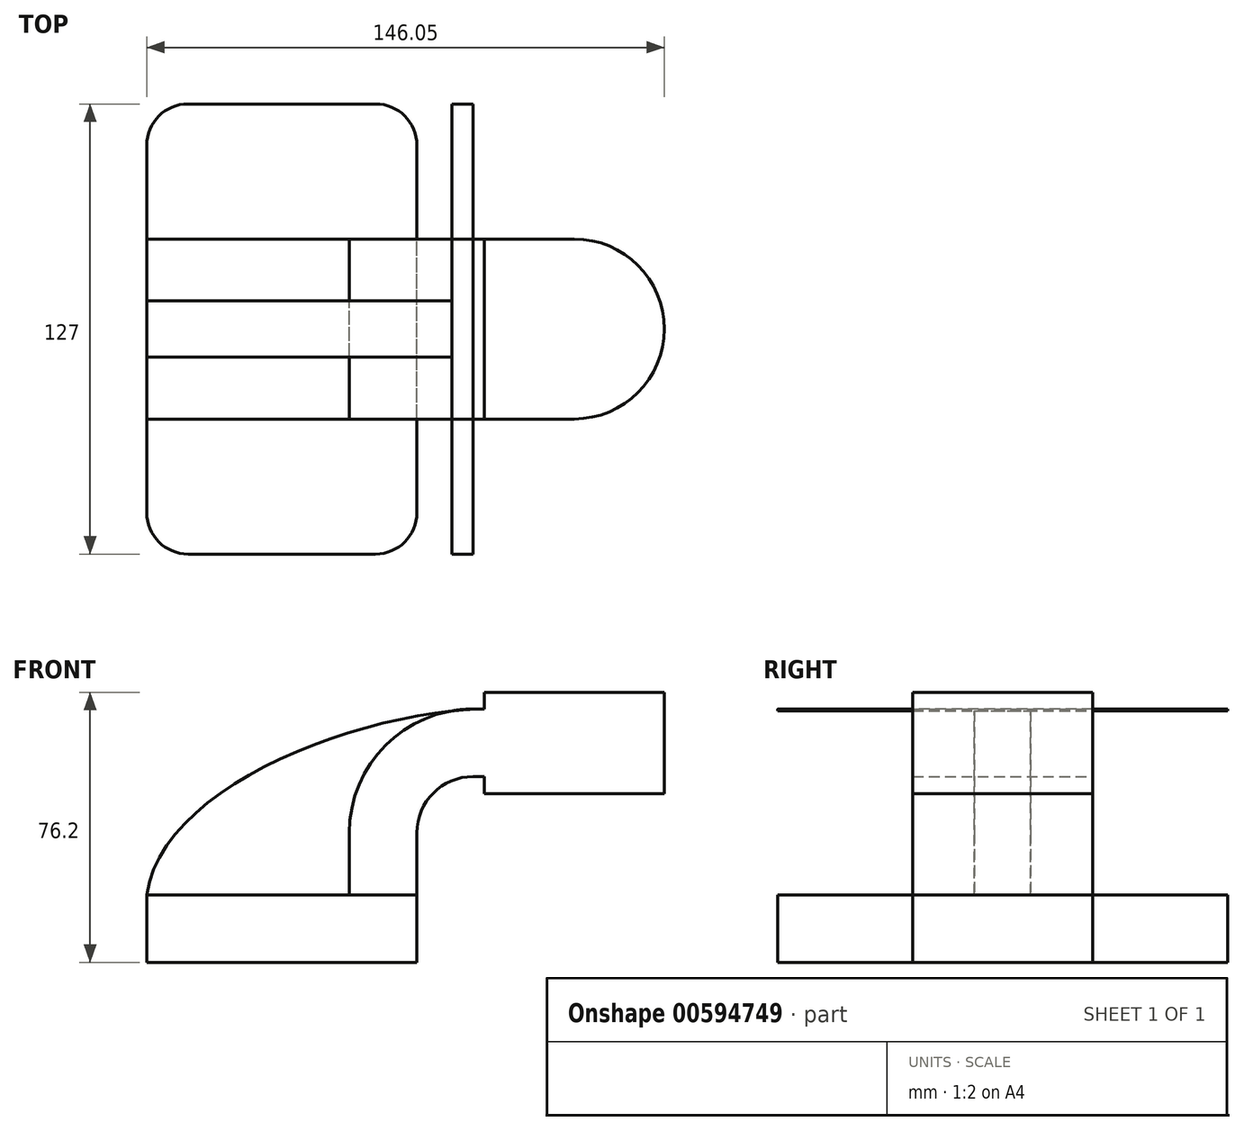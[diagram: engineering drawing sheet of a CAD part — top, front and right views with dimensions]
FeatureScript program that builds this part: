
annotation { "Feature Type Name" : "Feature", "Feature Type Description" : "" }
export const myFeature = defineFeature(function(context is Context, id is Id, definition is map)
    precondition{}
    {
        {
            var Q0;
            Q0=qCreatedBy(makeId("Front.planeOp"),FACE);
            var sketch = newSketch(context, id + "F0", { "sketchPlane" : qUnion([Q0])});
            skLineSegment(sketch, "E0.bottom", {"start": v(-38.1, 9.52) * mm, "end": v(38.1, 9.53) * mm});
            skLineSegment(sketch, "E0.top", {"start": v(-38.1, -9.53) * mm, "end": v(38.1, -9.53) * mm});
            skLineSegment(sketch, "E0.left", {"start": v(-38.1, 9.52) * mm, "end": v(-38.1, -9.53) * mm});
            skLineSegment(sketch, "E0.right", {"start": v(38.1, 9.53) * mm, "end": v(38.1, -9.52) * mm});
            skPoint(sketch, "E0.middle", {"position": v(0, 0) * mm});
            skLineSegment(sketch, "E1.bottom", {"start": v(107.95, 66.68) * mm, "end": v(57.15, 66.68) * mm});
            skLineSegment(sketch, "E1.top", {"start": v(107.95, 38.1) * mm, "end": v(57.15, 38.1) * mm});
            skLineSegment(sketch, "E1.left", {"start": v(107.95, 66.68) * mm, "end": v(107.95, 38.1) * mm});
            skLineSegment(sketch, "E1.right", {"start": v(57.15, 66.68) * mm, "end": v(57.15, 38.1) * mm});
            skPoint(sketch, "E1.middle", {"position": v(82.55, 52.39) * mm});
            skLineSegment(sketch, "E2", {"start": v(38.1, 9.53) * mm, "end": v(38.1, 27) * mm, "construction": true});
            skArc(sketch, "E3", {"start": v(53.97, 42.88) * mm, "mid": v(42.75, 38.23) * mm, "end": v(38.1, 27) * mm});
            skLineSegment(sketch, "E4", {"start": v(53.97, 42.88) * mm, "end": v(82.55, 42.88) * mm});
            skArc(sketch, "E5.0", {"start": v(53.97, 61.93) * mm, "mid": v(29.28, 51.7) * mm, "end": v(19.05, 27) * mm});
            skLineSegment(sketch, "E6", {"start": v(19.05, 27) * mm, "end": v(19.05, 9.53) * mm});
            skLineSegment(sketch, "E7", {"start": v(53.97, 61.93) * mm, "end": v(82.55, 61.93) * mm});
            skLineSegment(sketch, "E8", {"start": v(38.1, 27) * mm, "end": v(38.1, 9.53) * mm});
            skFitSpline(sketch, "E9", {"points": [v(-38.1, 9.52) * mm, v(53.97, 61.93) * mm], "startDerivative": vector(12.38, 88.95) * mm, "endDerivative": vector(109.97, 6.84) * mm});
            skLineSegment(sketch, "E10", {"start": v(82.55, 38.1) * mm, "end": v(82.55, 66.68) * mm});
            skSolve(sketch);
        }
        {
            var Q0;
            {var subQ0=sQuery(id+"F0.wireOp",EDGE,"E9");var subQ1=sQuery(id+"F0.wireOp",EDGE,"E5.0");var subQ3=makeQuery(id+"F0.imprint","INTERSECT",VERTEX,{"derivedFrom":[subQ1,subQ0]});Q0=makeQuery(id+"F0.imprint","IMPRINT",FACE,{"disambiguationData":[TD([[makeQuery(id+"F0.imprint","IMPRINT",EDGE,{"disambiguationData":[TD([[subQ3,1.0]])],"derivedFrom":subQ1}),1.0]])]});}
            var Q1;
            Q1=makeQuery(id+"F0.imprint","IMPRINT",FACE,{"disambiguationData":[TD([[makeQuery(id+"F0.imprint","IMPRINT",EDGE,{"derivedFrom":sQuery(id+"F0.wireOp",EDGE,"E0.top")}),1.0]])]});
            extrude(context, id + "F1", {"entities" : qUnion([Q0, Q1]), "depth" : 127 * mm, "offsetDistance" : 25.4 * mm, "symmetric" : true});
        }
        {
            var Q0;
            {var subQ0=sQuery(id+"F0.wireOp",EDGE,"E9");var subQ1=sQuery(id+"F0.wireOp",EDGE,"E5.0");var subQ3=makeQuery(id+"F0.imprint","INTERSECT",VERTEX,{"derivedFrom":[subQ1,subQ0]});Q0=makeQuery(id+"F0.imprint","IMPRINT",FACE,{"disambiguationData":[TD([[makeQuery(id+"F0.imprint","IMPRINT",EDGE,{"disambiguationData":[TD([[subQ3,1.0]])],"derivedFrom":subQ1}),1.0]])]});}
            var Q1;
            Q1=makeQuery(id+"F0.imprint","IMPRINT",FACE,{"disambiguationData":[TD([[makeQuery(id+"F0.imprint","IMPRINT",EDGE,{"derivedFrom":sQuery(id+"F0.wireOp",EDGE,"E0.top")}),1.0]])]});
            var Q2;
            {var subQ0=sQuery(id+"F0.wireOp",EDGE,"E1.right");var subQ1=sQuery(id+"F0.wireOp",EDGE,"E1.bottom");var subQ2=makeQuery(id+"F0.imprint","INTERSECT",VERTEX,{"derivedFrom":[subQ1,subQ0]});Q2=makeQuery(id+"F0.imprint","IMPRINT",FACE,{"disambiguationData":[TD([[makeQuery(id+"F0.imprint","IMPRINT",EDGE,{"disambiguationData":[TD([[subQ2,1.0]])],"derivedFrom":subQ1}),1.0]])]});}
            var Q3;
            {var subQ0=sQuery(id+"F0.wireOp",EDGE,"E1.right");var subQ1=sQuery(id+"F0.wireOp",EDGE,"E1.top");var subQ2=makeQuery(id+"F0.imprint","INTERSECT",VERTEX,{"derivedFrom":[subQ1,subQ0]});Q3=makeQuery(id+"F0.imprint","IMPRINT",FACE,{"disambiguationData":[TD([[makeQuery(id+"F0.imprint","IMPRINT",EDGE,{"disambiguationData":[TD([[subQ2,1.0]])],"derivedFrom":subQ1}),-1.0]])]});}
            var Q4;
            {var subQ0=sQuery(id+"F0.wireOp",EDGE,"E7");var subQ1=sQuery(id+"F0.wireOp",EDGE,"E1.right");var subQ2=makeQuery(id+"F0.imprint","INTERSECT",VERTEX,{"derivedFrom":[subQ1,subQ0]});Q4=makeQuery(id+"F0.imprint","IMPRINT",FACE,{"disambiguationData":[TD([[makeQuery(id+"F0.imprint","IMPRINT",EDGE,{"disambiguationData":[TD([[subQ2,-1.0]])],"derivedFrom":subQ1}),1.0]])]});}
            var Q5;
            {var subQ1=sQuery(id+"F0.wireOp",EDGE,"E3");Q5=makeQuery(id+"F0.imprint","IMPRINT",FACE,{"disambiguationData":[TD([[makeQuery(id+"F0.imprint","IMPRINT",EDGE,{"derivedFrom":subQ1}),-1.0]])]});}
            extrude(context, id + "F2", {"entities" : qUnion([Q0, Q1, Q2, Q3, Q4, Q5]), "depth" : 50.8 * mm, "offsetDistance" : 25.4 * mm, "symmetric" : true});
        }
        {
            var Q0;
            {var subQ3=sQuery(id+"F0.wireOp",EDGE,"E6");Q0=makeQuery(id+"F0.imprint","IMPRINT",FACE,{"disambiguationData":[TD([[makeQuery(id+"F0.imprint","IMPRINT",EDGE,{"derivedFrom":subQ3}),-1.0]])]});}
            extrude(context, id + "F3", {"entities" : qUnion([Q0]), "depth" : 15.88 * mm, "offsetDistance" : 25.4 * mm, "symmetric" : true});
        }
        {
            var Q0;
            Q0=makeQuery(id+"F1.opExtrude","CAP_EDGE",EDGE,{"disambiguationData":[OSD([sQuery(id+"F0.wireOp",EDGE,"E0.left")])],"isStart":true});
            var Q1;
            Q1=makeQuery(id+"F1.opExtrude","CAP_EDGE",EDGE,{"disambiguationData":[OSD([sQuery(id+"F0.wireOp",EDGE,"E0.right")])],"isStart":true});
            var Q2;
            Q2=makeQuery(id+"F1.opExtrude","CAP_EDGE",EDGE,{"disambiguationData":[OSD([sQuery(id+"F0.wireOp",EDGE,"E0.left")])],"isStart":false});
            var Q3;
            Q3=makeQuery(id+"F1.opExtrude","CAP_EDGE",EDGE,{"disambiguationData":[OSD([sQuery(id+"F0.wireOp",EDGE,"E0.right")])],"isStart":false});
            fillet(context, id + "F4", {"entities" : qUnion([Q0, Q1, Q2, Q3]), "radius" : 11.65 * mm, "tangentPropagation" : true, "allowEdgeOverflow" : false});
        }
        {
            var Q0;
            {var subQ4=sQuery(id+"F0.wireOp",EDGE,"E1.left");Q0=makeQuery(id+"F0.imprint","IMPRINT",FACE,{"disambiguationData":[TD([[makeQuery(id+"F0.imprint","IMPRINT",EDGE,{"derivedFrom":subQ4}),-1.0]])]});}
            var Q1;
            Q1=sQuery(id+"F0.wireOp",EDGE,"E10");
            revolve(context, id + "F5", {"operationType" : NewBodyOperationType.ADD, "entities" : qUnion([Q0]), "axis" : qUnion([Q1]), "revolveType" : RevolveType.FULL});
        }
    });
